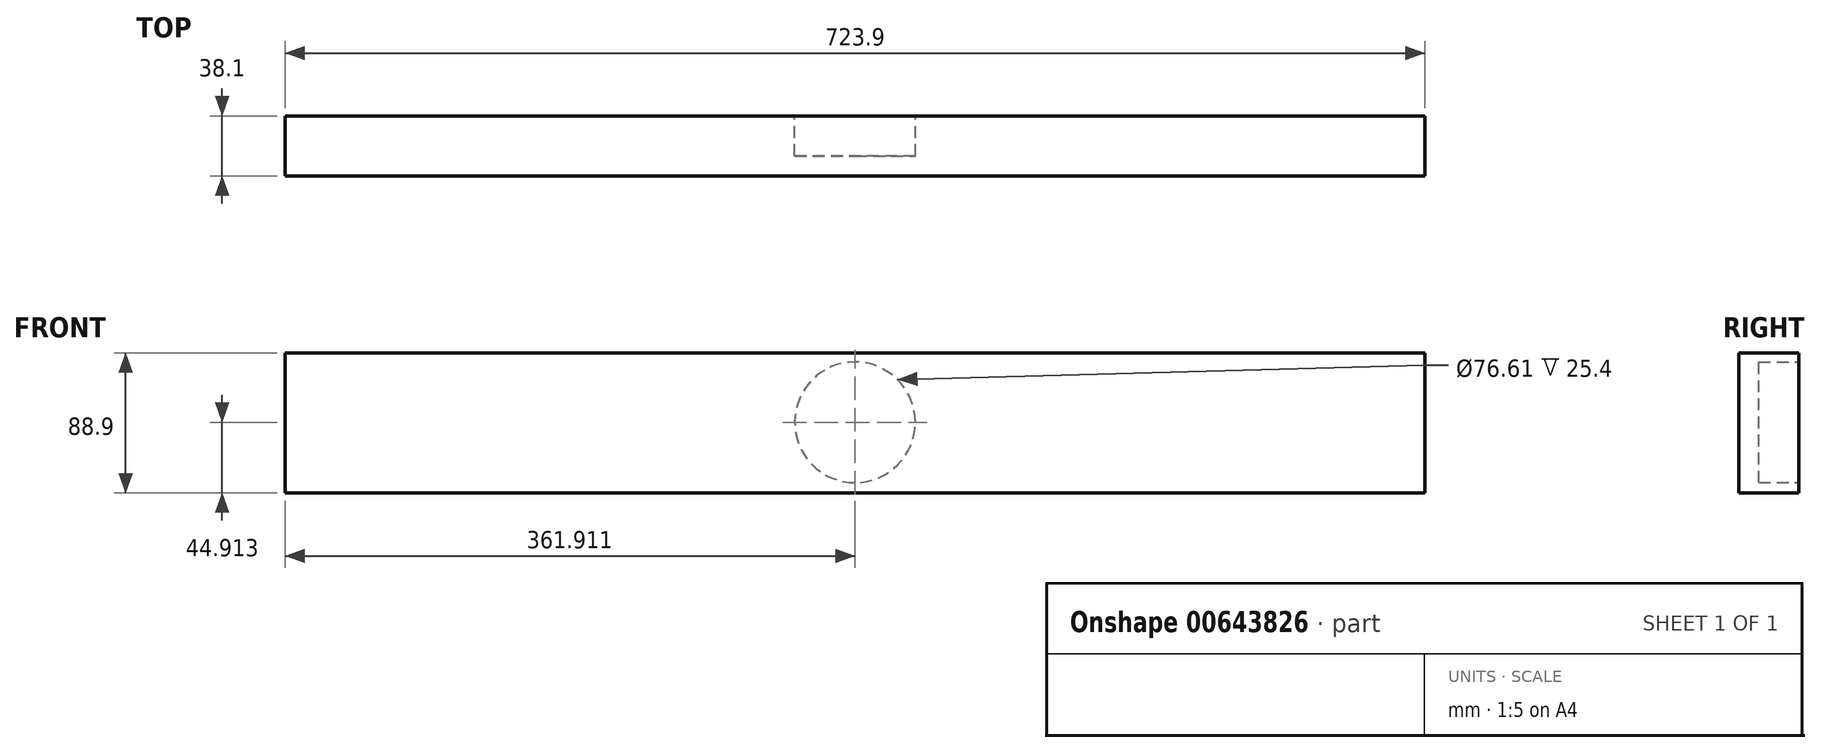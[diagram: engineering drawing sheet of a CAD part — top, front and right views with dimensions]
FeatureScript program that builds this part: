
annotation { "Feature Type Name" : "Feature", "Feature Type Description" : "" }
export const myFeature = defineFeature(function(context is Context, id is Id, definition is map)
    precondition{}
    {
        {
            var Q0;
            Q0=qCreatedBy(makeId("Front.planeOp"),FACE);
            var sketch = newSketch(context, id + "F0", { "sketchPlane" : qUnion([Q0])});
            skLineSegment(sketch, "E0.bottom", {"start": v(-148.73, 56.16) * mm, "end": v(575.17, 56.16) * mm});
            skLineSegment(sketch, "E0.top", {"start": v(-148.73, -32.74) * mm, "end": v(575.17, -32.74) * mm});
            skLineSegment(sketch, "E0.left", {"start": v(-148.73, 56.16) * mm, "end": v(-148.73, -32.74) * mm});
            skLineSegment(sketch, "E0.right", {"start": v(575.17, 56.16) * mm, "end": v(575.17, -32.74) * mm});
            skSolve(sketch);
        }
        {
            var Q0;
            Q0=makeQuery(id+"F0.imprint","IMPRINT",FACE,{"disambiguationData":[TD([[makeQuery(id+"F0.imprint","IMPRINT",EDGE,{"derivedFrom":sQuery(id+"F0.wireOp",EDGE,"E0.bottom")}),-1.0]])]});
            extrude(context, id + "F1", {"entities" : qUnion([Q0]), "depth" : 38.1 * mm, "offsetDistance" : 25.4 * mm});
        }
        {
            var Q0;
            Q0=makeQuery(id+"F0.imprint","IMPRINT",FACE,{"disambiguationData":[TD([[makeQuery(id+"F0.imprint","IMPRINT",EDGE,{"derivedFrom":sQuery(id+"F0.wireOp",EDGE,"E0.bottom")}),-1.0]])]});
            var sketch = newSketch(context, id + "F2", { "sketchPlane" : qUnion([Q0])});
            skCircle(sketch, "E1", {"center": v(213.18, 12.17) * mm, "radius": 38.3 * mm});
            skSolve(sketch);
        }
        {
            var Q0;
            Q0=makeQuery(id+"F2.imprint","IMPRINT",FACE,{"disambiguationData":[TD([[makeQuery(id+"F2.imprint","IMPRINT",EDGE,{"derivedFrom":sQuery(id+"F2.wireOp",EDGE,"E1")}),1.0]])]});
            var Q1;
            Q1=sQuery(id+"F2.wireOp",EDGE,"E1");
            extrude(context, id + "F3", {"entities" : qUnion([Q0]), "operationType" : NewBodyOperationType.REMOVE, "surfaceEntities" : qUnion([Q1]), "oppositeDirection" : true, "depth" : -25.4 * mm, "offsetDistance" : 25.4 * mm});
        }
    });
